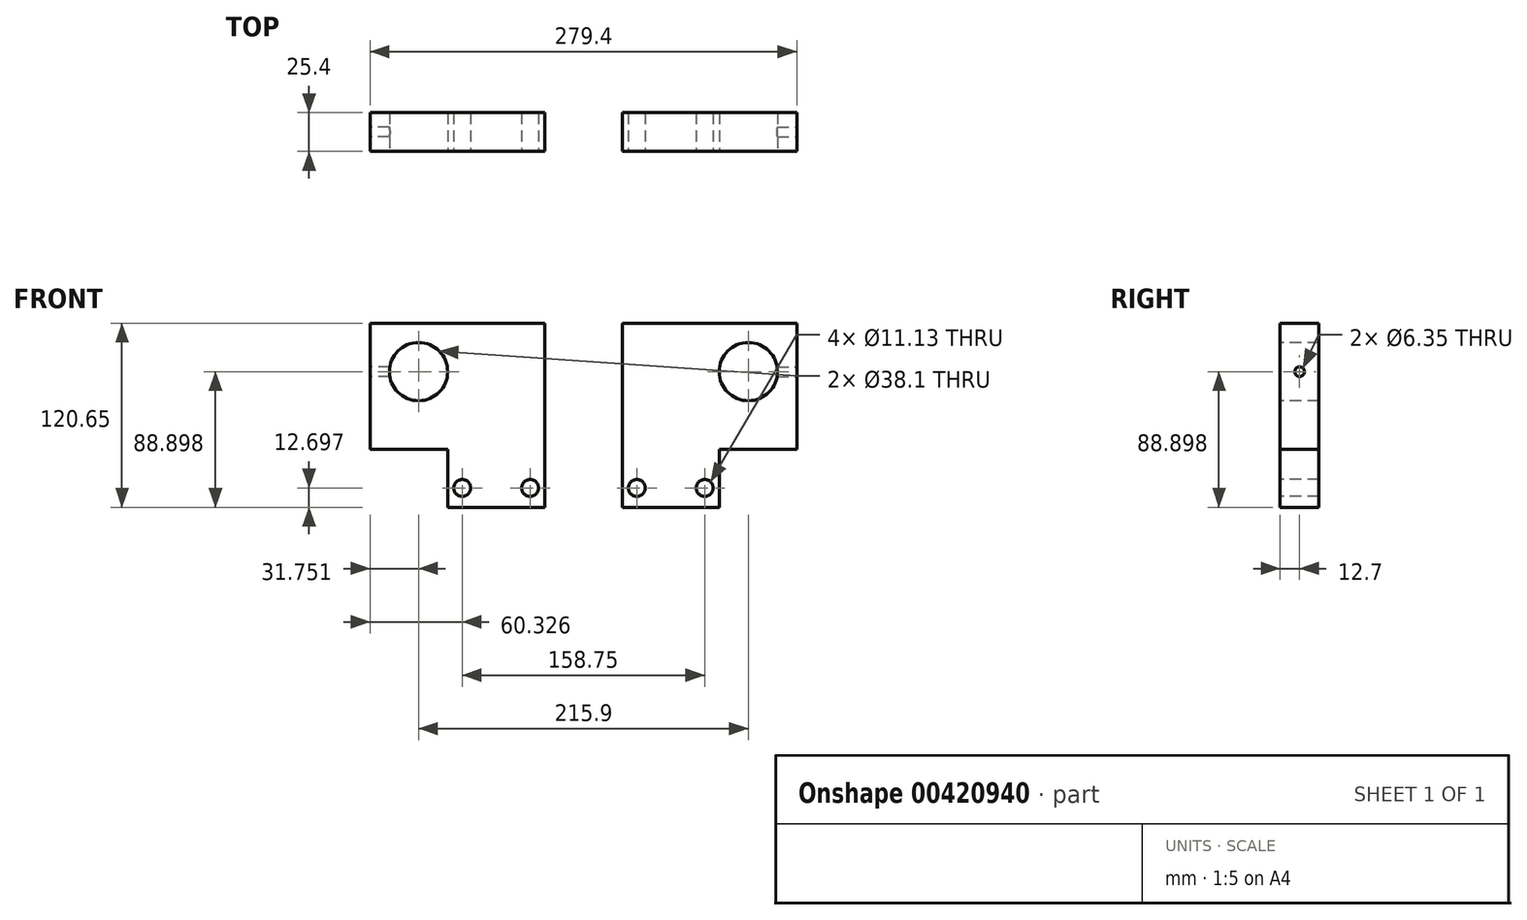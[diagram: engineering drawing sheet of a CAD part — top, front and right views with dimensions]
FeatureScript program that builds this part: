
annotation { "Feature Type Name" : "Feature", "Feature Type Description" : "" }
export const myFeature = defineFeature(function(context is Context, id is Id, definition is map)
    precondition{}
    {
        {
            var Q0;
            Q0=qCreatedBy(makeId("Front.planeOp"),FACE);
            var sketch = newSketch(context, id + "F0", { "sketchPlane" : qUnion([Q0])});
            skLineSegment(sketch, "E0.bottom", {"start": v(1386.2, -868) * mm, "end": v(1449.7, -868) * mm});
            skLineSegment(sketch, "E0.top", {"start": v(1386.2, -988.64) * mm, "end": v(1449.7, -988.64) * mm});
            skLineSegment(sketch, "E0.left", {"start": v(1386.2, -868) * mm, "end": v(1386.2, -988.64) * mm});
            skLineSegment(sketch, "E0.right", {"start": v(1449.7, -950.54) * mm, "end": v(1449.7, -988.64) * mm});
            skLineSegment(sketch, "E1.bottom", {"start": v(1449.7, -868) * mm, "end": v(1500.5, -868) * mm});
            skLineSegment(sketch, "E1.top", {"start": v(1449.7, -950.54) * mm, "end": v(1500.5, -950.54) * mm});
            skLineSegment(sketch, "E1.right", {"start": v(1500.5, -868) * mm, "end": v(1500.5, -950.54) * mm});
            skCircle(sketch, "E2", {"center": v(1468.75, -899.74) * mm, "radius": 19.05 * mm});
            skCircle(sketch, "E3", {"center": v(1395.73, -975.94) * mm, "radius": 5.56 * mm});
            skCircle(sketch, "E4", {"center": v(1440.18, -975.94) * mm, "radius": 5.56 * mm});
            skSolve(sketch);
        }
        {
            var Q0;
            Q0 = qSketchRegion(id + "F0", true);
            extrude(context, id + "F1", {"entities" : qUnion([Q0]), "oppositeDirection" : true, "depth" : 25.4 * mm});
        }
        {
            var Q0;
            Q0=makeQuery(id+"F1.opExtrude","SWEPT_FACE",FACE,{"disambiguationData":[OSD([sQuery(id+"F0.wireOp",EDGE,"E1.right")])]});
            var sketch = newSketch(context, id + "F2", { "sketchPlane" : qUnion([Q0])});
            skCircle(sketch, "E5", {"center": v(12.7, -899.74) * mm, "radius": 3.18 * mm});
            skSolve(sketch);
        }
        {
            var Q0;
            Q0 = qSketchRegion(id + "F2", true);
            extrude(context, id + "F3", {"entities" : qUnion([Q0]), "operationType" : NewBodyOperationType.REMOVE, "oppositeDirection" : true, "depth" : 25.4 * mm});
        }
        {
            var Q0;
            Q0=makeQuery(id+"F1.opExtrude","SWEPT_FACE",FACE,{"disambiguationData":[OSD([sQuery(id+"F0.wireOp",EDGE,"E0.left")])]});
            cPlane(context, id + "F4", {"entities" : qUnion([Q0]), "cplaneType" : CPlaneType.OFFSET, "offset" : 25.4 * mm, "width" : 152.4 * mm, "height" : 152.4 * mm});
        }
        {
            var Q0;
            Q0=makeQuery(id+"F1.opExtrude","SWEPT_BODY",BODY,{"disambiguationData":[OSD([sQuery(id+"F0.wireOp",EDGE,"E0.bottom"),sQuery(id+"F0.wireOp",EDGE,"E0.top"),sQuery(id+"F0.wireOp",EDGE,"E0.left"),sQuery(id+"F0.wireOp",EDGE,"E0.right"),sQuery(id+"F0.wireOp",EDGE,"E1.bottom"),sQuery(id+"F0.wireOp",EDGE,"E1.top"),sQuery(id+"F0.wireOp",EDGE,"E1.right"),sQuery(id+"F0.wireOp",EDGE,"E2"),sQuery(id+"F0.wireOp",EDGE,"E3"),sQuery(id+"F0.wireOp",EDGE,"E4")])]});
            var Q1;
            Q1=qCreatedBy(id+"F4.planeOp",FACE);
            mirror(context, id + "F5", {"entities" : qUnion([Q0]), "mirrorPlane" : qUnion([Q1])});
        }
    });
